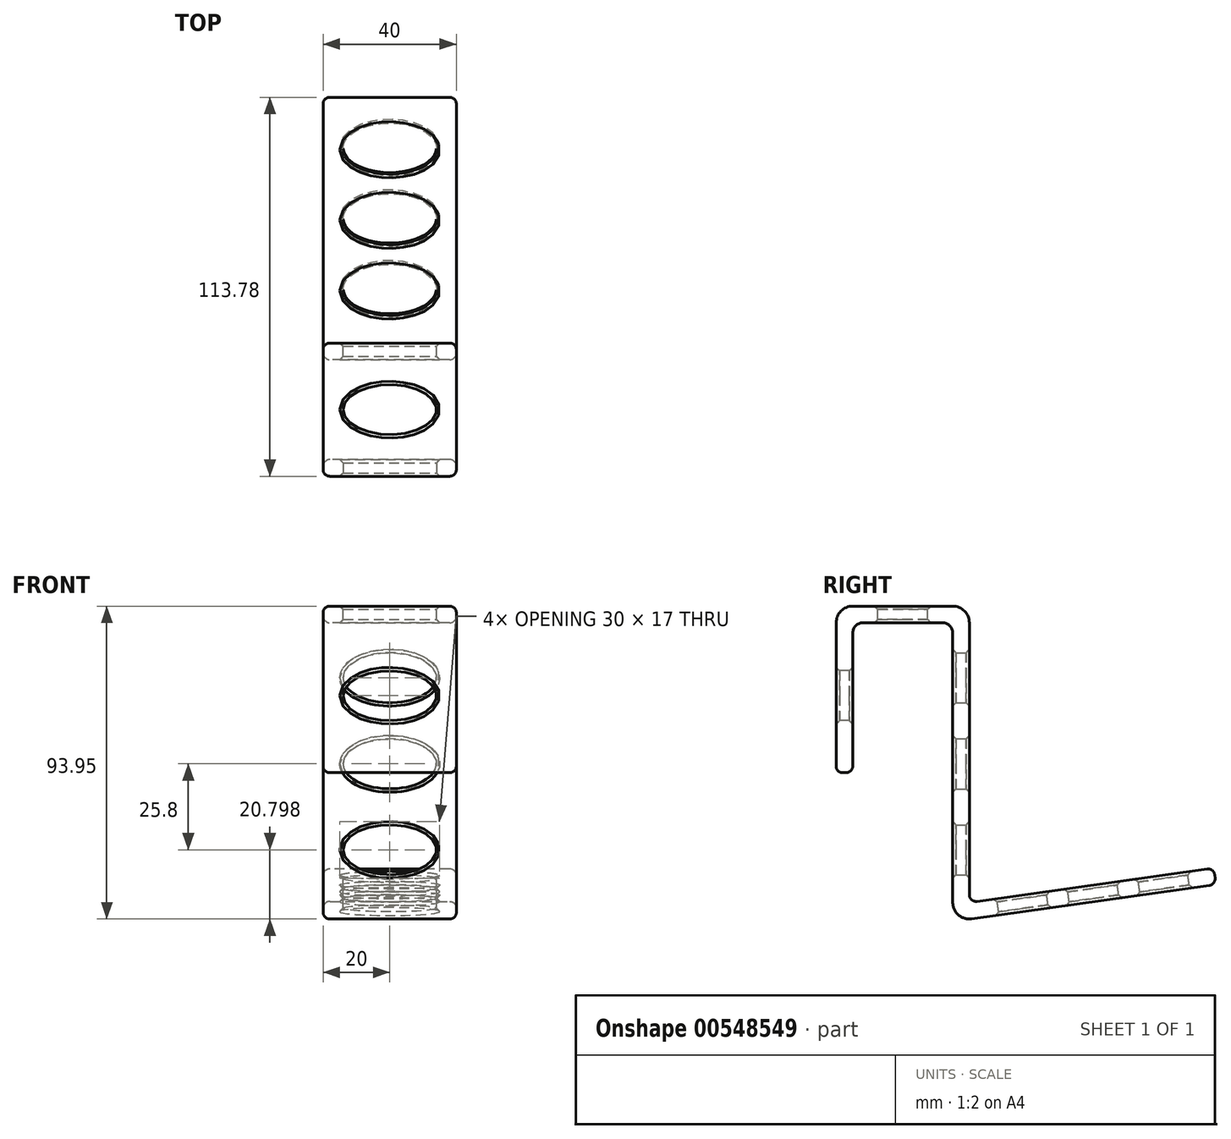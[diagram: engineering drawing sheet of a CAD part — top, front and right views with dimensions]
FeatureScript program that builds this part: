
annotation { "Feature Type Name" : "Feature", "Feature Type Description" : "" }
export const myFeature = defineFeature(function(context is Context, id is Id, definition is map)
    precondition{}
    {
        {
            var Q0;
            Q0=qCreatedBy(makeId("Right.planeOp"),FACE);
            var sketch = newSketch(context, id + "F0", { "sketchPlane" : qUnion([Q0])});
            skLineSegment(sketch, "E0", {"start": v(-12, 0) * mm, "end": v(12, 0) * mm});
            skLineSegment(sketch, "E1", {"start": v(15, -3) * mm, "end": v(15, -89.7) * mm});
            skLineSegment(sketch, "E2", {"start": v(15, -89.7) * mm, "end": v(93.93, -78.61) * mm});
            skLineSegment(sketch, "E3", {"start": v(-15, -3) * mm, "end": v(-15, -45) * mm});
            skLineSegment(sketch, "E4.0", {"start": v(20, -83.95) * mm, "end": v(93.5, -73.62) * mm});
            skLineSegment(sketch, "E4.1", {"start": v(20, 5) * mm, "end": v(20, -83.95) * mm});
            skLineSegment(sketch, "E4.2", {"start": v(-20, 5) * mm, "end": v(20, 5) * mm});
            skLineSegment(sketch, "E4.3", {"start": v(-20, 5) * mm, "end": v(-20, -45) * mm});
            skLineSegment(sketch, "E5", {"start": v(-15, -45) * mm, "end": v(-20, -45) * mm});
            skLineSegment(sketch, "E6", {"start": v(93.5, -73.62) * mm, "end": v(93.93, -78.61) * mm});
            skPoint(sketch, "E7.visualSharp", {"position": v(-15, 0) * mm});
            skArc(sketch, "E7.filletArc", {"start": v(-12, 0) * mm, "mid": v(-14.12, -0.88) * mm, "end": v(-15, -3) * mm});
            skPoint(sketch, "E8.visualSharp", {"position": v(15, 0) * mm});
            skArc(sketch, "E8.filletArc", {"start": v(15, -3) * mm, "mid": v(14.12, -0.88) * mm, "end": v(12, 0) * mm});
            skSolve(sketch);
        }
        {
            var Q0;
            Q0 = qSketchRegion(id + "F0", true);
            extrude(context, id + "F1", {"entities" : qUnion([Q0]), "depth" : 40 * mm, "offsetDistance" : 25 * mm});
        }
        {
            var Q0;
            Q0=makeQuery(id+"F1.opExtrude","SWEPT_EDGE",EDGE,{"disambiguationData":[OSD([sQuery(id+"F0.wireOp",EDGE,"E4.1"),sQuery(id+"F0.wireOp",EDGE,"E4.2")])]});
            var Q1;
            Q1=makeQuery(id+"F1.opExtrude","SWEPT_EDGE",EDGE,{"disambiguationData":[OSD([sQuery(id+"F0.wireOp",EDGE,"E4.2"),sQuery(id+"F0.wireOp",EDGE,"E4.3")])]});
            var Q2;
            Q2=makeQuery(id+"F1.opExtrude","SWEPT_EDGE",EDGE,{"disambiguationData":[OSD([sQuery(id+"F0.wireOp",EDGE,"E1"),sQuery(id+"F0.wireOp",EDGE,"E2")])]});
            fillet(context, id + "F2", {"entities" : qUnion([Q0, Q1, Q2]), "radius" : 5 * mm, "tangentPropagation" : true, "allowEdgeOverflow" : false});
        }
        {
            var Q0;
            Q0=makeQuery(id+"F1.opExtrude","SWEPT_EDGE",EDGE,{"disambiguationData":[OSD([sQuery(id+"F0.wireOp",EDGE,"E4.0"),sQuery(id+"F0.wireOp",EDGE,"E4.1")])]});
            fillet(context, id + "F3", {"entities" : qUnion([Q0]), "radius" : 2 * mm, "tangentPropagation" : true, "allowEdgeOverflow" : false});
        }
        {
            var Q0;
            Q0=makeQuery(id+"F1.opExtrude","SWEPT_EDGE",EDGE,{"disambiguationData":[OSD([sQuery(id+"F0.wireOp",EDGE,"E4.3"),sQuery(id+"F0.wireOp",EDGE,"E5")])]});
            var Q1;
            Q1=makeQuery(id+"F1.opExtrude","SWEPT_EDGE",EDGE,{"disambiguationData":[OSD([sQuery(id+"F0.wireOp",EDGE,"E3"),sQuery(id+"F0.wireOp",EDGE,"E5")])]});
            var Q2;
            Q2=makeQuery(id+"F1.opExtrude","SWEPT_EDGE",EDGE,{"disambiguationData":[OSD([sQuery(id+"F0.wireOp",EDGE,"E4.0"),sQuery(id+"F0.wireOp",EDGE,"E6")])]});
            var Q3;
            Q3=makeQuery(id+"F1.opExtrude","SWEPT_EDGE",EDGE,{"disambiguationData":[OSD([sQuery(id+"F0.wireOp",EDGE,"E2"),sQuery(id+"F0.wireOp",EDGE,"E6")])]});
            var Q4;
            Q4=makeQuery(id+"F1.opExtrude","CAP_FACE",FACE,{"disambiguationData":[OSD([sQuery(id+"F0.wireOp",EDGE,"E0"),sQuery(id+"F0.wireOp",EDGE,"E1"),sQuery(id+"F0.wireOp",EDGE,"E2"),sQuery(id+"F0.wireOp",EDGE,"E3"),sQuery(id+"F0.wireOp",EDGE,"E4.0"),sQuery(id+"F0.wireOp",EDGE,"E4.1"),sQuery(id+"F0.wireOp",EDGE,"E4.2"),sQuery(id+"F0.wireOp",EDGE,"E4.3"),sQuery(id+"F0.wireOp",EDGE,"E5"),sQuery(id+"F0.wireOp",EDGE,"E6"),sQuery(id+"F0.wireOp",EDGE,"E7.filletArc"),sQuery(id+"F0.wireOp",EDGE,"E8.filletArc")])],"isStart":false});
            var Q5;
            Q5=makeQuery(id+"F1.opExtrude","CAP_FACE",FACE,{"disambiguationData":[OSD([sQuery(id+"F0.wireOp",EDGE,"E0"),sQuery(id+"F0.wireOp",EDGE,"E1"),sQuery(id+"F0.wireOp",EDGE,"E2"),sQuery(id+"F0.wireOp",EDGE,"E3"),sQuery(id+"F0.wireOp",EDGE,"E4.0"),sQuery(id+"F0.wireOp",EDGE,"E4.1"),sQuery(id+"F0.wireOp",EDGE,"E4.2"),sQuery(id+"F0.wireOp",EDGE,"E4.3"),sQuery(id+"F0.wireOp",EDGE,"E5"),sQuery(id+"F0.wireOp",EDGE,"E6"),sQuery(id+"F0.wireOp",EDGE,"E7.filletArc"),sQuery(id+"F0.wireOp",EDGE,"E8.filletArc")])],"isStart":true});
            fillet(context, id + "F4", {"entities" : qUnion([Q0, Q1, Q2, Q3, Q4, Q5]), "radius" : 2 * mm, "tangentPropagation" : true, "allowEdgeOverflow" : false});
        }
        {
            var Q0;
            Q0=makeQuery(id+"F1.opExtrude","SWEPT_FACE",FACE,{"disambiguationData":[OSD([sQuery(id+"F0.wireOp",EDGE,"E4.2")])]});
            var sketch = newSketch(context, id + "F5", { "sketchPlane" : qUnion([Q0])});
            skPoint(sketch, "E9.centerSnap0", {"position": v(20, 15) * mm});
            skEllipse(sketch, "E10", {"center": v(20, 0) * mm, "majorRadius": 14 * mm, "minorRadius": 7.5 * mm, "majorAxis": v(-1, 0)});
            skSolve(sketch);
        }
        {
            var Q0;
            Q0=makeQuery(id+"F1.opExtrude","SWEPT_FACE",FACE,{"disambiguationData":[OSD([sQuery(id+"F0.wireOp",EDGE,"E4.0")])]});
            var sketch = newSketch(context, id + "F6", { "sketchPlane" : qUnion([Q0])});
            skEllipse(sketch, "E11", {"center": v(20, 66.73) * mm, "majorRadius": 14 * mm, "minorRadius": 7.5 * mm, "majorAxis": v(-1, 0)});
            skPoint(sketch, "E11.centerSnap0", {"position": v(20, 80.23) * mm});
            skEllipse(sketch, "E12", {"center": v(20, 23.92) * mm, "majorRadius": 14 * mm, "minorRadius": 7.5 * mm, "majorAxis": v(-1, 0)});
            skPoint(sketch, "E12.centerSnap0", {"position": v(20, 59.23) * mm});
            skEllipse(sketch, "E13", {"center": v(20, 45.33) * mm, "majorRadius": 14 * mm, "minorRadius": 7.5 * mm, "majorAxis": v(-1, 0)});
            skPoint(sketch, "E13.centerSnap0", {"position": v(2, 45.33) * mm});
            skSolve(sketch);
        }
        {
            var Q0;
            Q0=makeQuery(id+"F1.opExtrude","SWEPT_FACE",FACE,{"disambiguationData":[OSD([sQuery(id+"F0.wireOp",EDGE,"E4.1")])]});
            var sketch = newSketch(context, id + "F7", { "sketchPlane" : qUnion([Q0])});
            skEllipse(sketch, "E14", {"center": v(-20, -16.5) * mm, "majorRadius": 14 * mm, "minorRadius": 7.5 * mm, "majorAxis": v(1, 0)});
            skPoint(sketch, "E14.centerSnap0", {"position": v(-20, 0) * mm});
            skEllipse(sketch, "E15", {"center": v(-20, -68.15) * mm, "majorRadius": 14 * mm, "minorRadius": 7.5 * mm, "majorAxis": v(1, 0)});
            skPoint(sketch, "E15.centerSnap0", {"position": v(-20, -81.65) * mm});
            skEllipse(sketch, "E16.0.1.0", {"center": v(-20, -42.35) * mm, "majorRadius": 14 * mm, "minorRadius": 7.5 * mm, "majorAxis": v(1, 0)});
            skLineSegment(sketch, "E16.direction1", {"start": v(-20, -68.15) * mm, "end": v(-7.2, -68.15) * mm, "construction": true});
            skLineSegment(sketch, "E16.direction2", {"start": v(-20, -68.15) * mm, "end": v(-20, -42.35) * mm, "construction": true});
            skSolve(sketch);
        }
        {
            var Q0;
            Q0=makeQuery(id+"F1.opExtrude","SWEPT_FACE",FACE,{"disambiguationData":[OSD([sQuery(id+"F0.wireOp",EDGE,"E4.3")])]});
            var sketch = newSketch(context, id + "F8", { "sketchPlane" : qUnion([Q0])});
            skEllipse(sketch, "E17", {"center": v(20, -21.9) * mm, "majorRadius": 14 * mm, "minorRadius": 7.5 * mm, "majorAxis": v(-1, 0)});
            skPoint(sketch, "E17.centerSnap0", {"position": v(2, -21.5) * mm});
            skPoint(sketch, "E17.centerSnap1", {"position": v(20, -43) * mm});
            skSolve(sketch);
        }
        {
            var Q0;
            Q0=makeQuery(id+"F8.imprint","IMPRINT",FACE,{"disambiguationData":[TD([[makeQuery(id+"F8.imprint","IMPRINT",EDGE,{"derivedFrom":sQuery(id+"F8.wireOp",EDGE,"E17")}),1.0]])]});
            var Q1;
            Q1=sQuery(id+"F8.wireOp",EDGE,"E17");
            var Q2;
            Q2=sQuery(id+"F5.wireOp",EDGE,"E10");
            var Q3;
            Q3=sQuery(id+"F7.wireOp",EDGE,"E14");
            var Q4;
            Q4=sQuery(id+"F7.wireOp",EDGE,"E16.0.1.0");
            var Q5;
            Q5=sQuery(id+"F7.wireOp",EDGE,"E15");
            var Q6;
            Q6=sQuery(id+"F6.wireOp",EDGE,"E12");
            var Q7;
            Q7=sQuery(id+"F6.wireOp",EDGE,"E13");
            var Q8;
            Q8=sQuery(id+"F6.wireOp",EDGE,"E11");
            extrude(context, id + "F9", {"entities" : qUnion([Q0]), "operationType" : NewBodyOperationType.REMOVE, "surfaceEntities" : qUnion([Q1, Q2, Q3, Q4, Q5, Q6, Q7, Q8]), "oppositeDirection" : true, "depth" : 6 * mm, "offsetDistance" : 25 * mm});
        }
        {
            var Q0;
            Q0=makeQuery(id+"F5.imprint","IMPRINT",FACE,{"disambiguationData":[TD([[makeQuery(id+"F5.imprint","IMPRINT",EDGE,{"derivedFrom":sQuery(id+"F5.wireOp",EDGE,"E10")}),1.0]])]});
            var Q1;
            Q1=sQuery(id+"F5.wireOp",EDGE,"E10");
            extrude(context, id + "F10", {"entities" : qUnion([Q0]), "operationType" : NewBodyOperationType.REMOVE, "surfaceEntities" : qUnion([Q1]), "oppositeDirection" : true, "depth" : 6 * mm, "offsetDistance" : 25 * mm});
        }
        {
            var Q0;
            Q0=makeQuery(id+"F6.imprint","IMPRINT",FACE,{"disambiguationData":[TD([[makeQuery(id+"F6.imprint","IMPRINT",EDGE,{"derivedFrom":sQuery(id+"F6.wireOp",EDGE,"E12")}),1.0]])]});
            var Q1;
            Q1=makeQuery(id+"F6.imprint","IMPRINT",FACE,{"disambiguationData":[TD([[makeQuery(id+"F6.imprint","IMPRINT",EDGE,{"derivedFrom":sQuery(id+"F6.wireOp",EDGE,"E13")}),1.0]])]});
            var Q2;
            Q2=makeQuery(id+"F6.imprint","IMPRINT",FACE,{"disambiguationData":[TD([[makeQuery(id+"F6.imprint","IMPRINT",EDGE,{"derivedFrom":sQuery(id+"F6.wireOp",EDGE,"E11")}),1.0]])]});
            extrude(context, id + "F11", {"entities" : qUnion([Q0, Q1, Q2]), "operationType" : NewBodyOperationType.REMOVE, "oppositeDirection" : true, "depth" : 6 * mm, "offsetDistance" : 25 * mm});
        }
        {
            var Q0;
            Q0=makeQuery(id+"F7.imprint","IMPRINT",FACE,{"disambiguationData":[TD([[makeQuery(id+"F7.imprint","IMPRINT",EDGE,{"derivedFrom":sQuery(id+"F7.wireOp",EDGE,"E14")}),1.0]])]});
            var Q1;
            Q1=makeQuery(id+"F7.imprint","IMPRINT",FACE,{"disambiguationData":[TD([[makeQuery(id+"F7.imprint","IMPRINT",EDGE,{"derivedFrom":sQuery(id+"F7.wireOp",EDGE,"E16.0.1.0")}),1.0]])]});
            var Q2;
            Q2=makeQuery(id+"F7.imprint","IMPRINT",FACE,{"disambiguationData":[TD([[makeQuery(id+"F7.imprint","IMPRINT",EDGE,{"derivedFrom":sQuery(id+"F7.wireOp",EDGE,"E15")}),1.0]])]});
            extrude(context, id + "F12", {"entities" : qUnion([Q0, Q1, Q2]), "operationType" : NewBodyOperationType.REMOVE, "oppositeDirection" : true, "depth" : 6 * mm, "offsetDistance" : 25 * mm});
        }
        {
            var Q0;
            Q0=makeQuery(id+"F9.boolean.opBoolean","COPY",FACE,{"derivedFrom":makeQuery(id+"F9.opExtrude","SWEPT_FACE",FACE,{"disambiguationData":[OSD([sQuery(id+"F8.wireOp",EDGE,"E17")])]})});
            var Q1;
            Q1=makeQuery(id+"F10.boolean.opBoolean","COPY",FACE,{"derivedFrom":makeQuery(id+"F10.opExtrude","SWEPT_FACE",FACE,{"disambiguationData":[OSD([sQuery(id+"F5.wireOp",EDGE,"E10")])]})});
            var Q2;
            Q2=makeQuery(id+"F12.boolean.opBoolean","COPY",FACE,{"derivedFrom":makeQuery(id+"F12.opExtrude","SWEPT_FACE",FACE,{"disambiguationData":[OSD([sQuery(id+"F7.wireOp",EDGE,"E14")])]})});
            var Q3;
            Q3=makeQuery(id+"F12.boolean.opBoolean","COPY",FACE,{"derivedFrom":makeQuery(id+"F12.opExtrude","SWEPT_FACE",FACE,{"disambiguationData":[OSD([sQuery(id+"F7.wireOp",EDGE,"E16.0.1.0")])]})});
            var Q4;
            Q4=makeQuery(id+"F12.boolean.opBoolean","COPY",FACE,{"derivedFrom":makeQuery(id+"F12.opExtrude","SWEPT_FACE",FACE,{"disambiguationData":[OSD([sQuery(id+"F7.wireOp",EDGE,"E15")])]})});
            var Q5;
            Q5=makeQuery(id+"F11.boolean.opBoolean","COPY",FACE,{"derivedFrom":makeQuery(id+"F11.opExtrude","SWEPT_FACE",FACE,{"disambiguationData":[OSD([sQuery(id+"F6.wireOp",EDGE,"E12")])]})});
            var Q6;
            Q6=makeQuery(id+"F11.boolean.opBoolean","COPY",FACE,{"derivedFrom":makeQuery(id+"F11.opExtrude","SWEPT_FACE",FACE,{"disambiguationData":[OSD([sQuery(id+"F6.wireOp",EDGE,"E13")])]})});
            var Q7;
            Q7=makeQuery(id+"F11.boolean.opBoolean","COPY",FACE,{"derivedFrom":makeQuery(id+"F11.opExtrude","SWEPT_FACE",FACE,{"disambiguationData":[OSD([sQuery(id+"F6.wireOp",EDGE,"E11")])]})});
            chamfer(context, id + "F13", {"entities" : qUnion([Q0, Q1, Q2, Q3, Q4, Q5, Q6, Q7]), "width" : 1 * mm, "tangentPropagation" : true});
        }
    });
